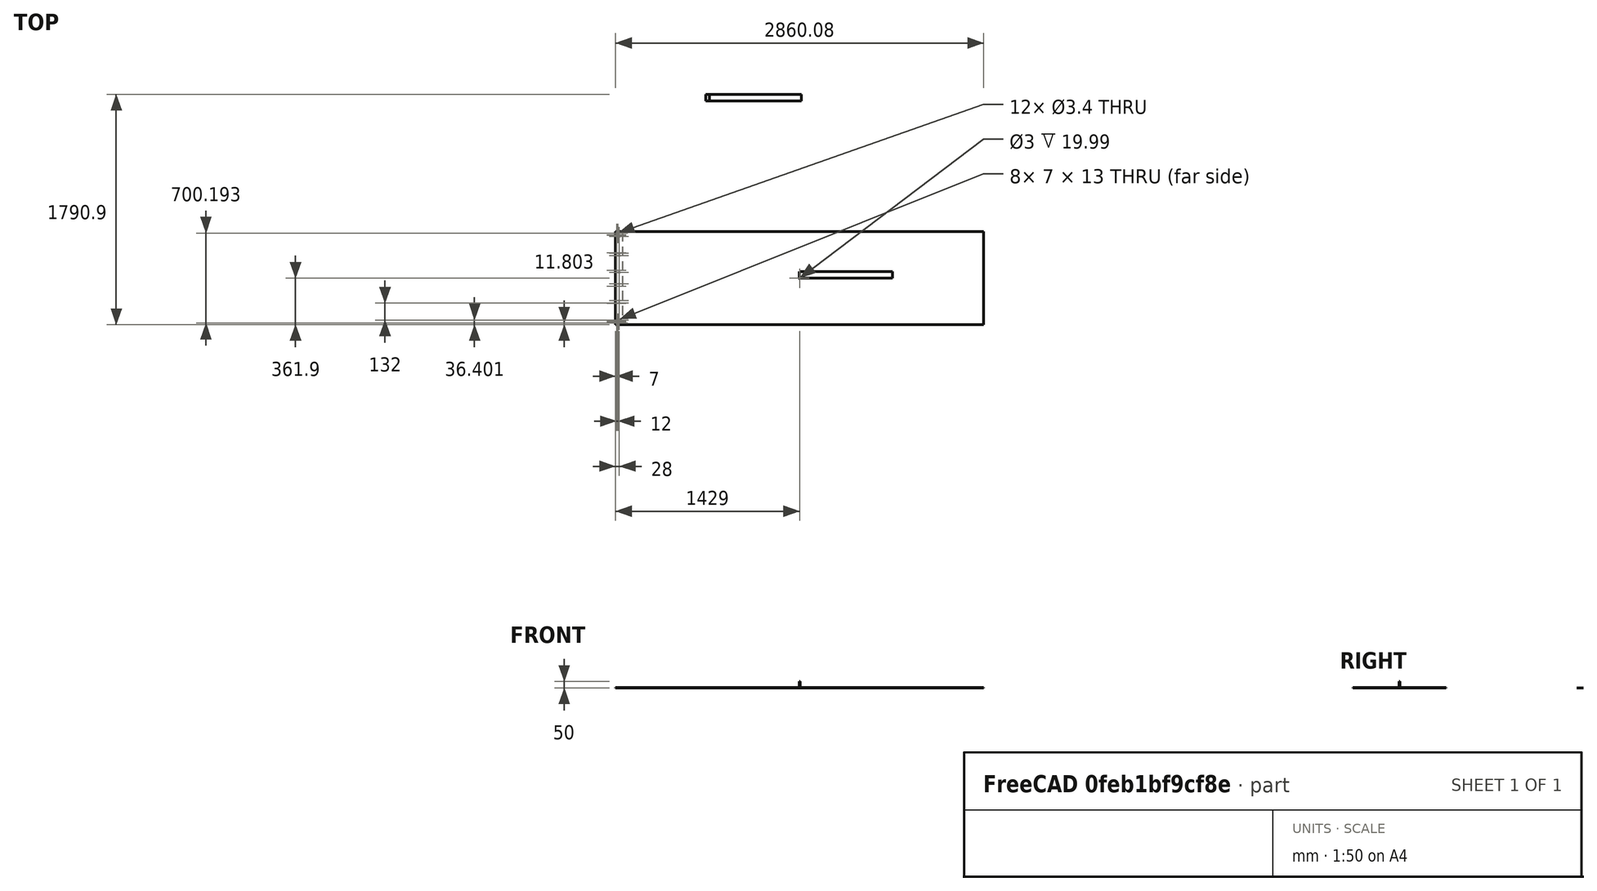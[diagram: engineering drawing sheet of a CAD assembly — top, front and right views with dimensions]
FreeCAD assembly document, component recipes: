
FREECAD ASSEMBLY — COMPONENT RECIPES ("composit3_top_amplifier_test")

This assembly document has 4 components, labeled P0..P3 below (a component is one placed body or linked part). 0 of them carry a construction recipe — the FreeCAD feature program that regenerates the part from scratch, quoted from this document or its linked companion documents; the rest are supplied as boundary geometry only. No exploded tour is included for this assembly.
COMPONENT P0 — geometry summary ("Body"; no construction recipe available for this part):
  bounding box: 721.8 x 50.0 x 0.3 mm
  tessellated surface: 852 triangles
  volume: 10573 mm^3 (98% of its bounding box)
  symmetry: 2-fold rotationally symmetric about the x axis; 2-fold rotationally symmetric about the y axis; 2-fold rotationally symmetric about the z axis; mirror-symmetric across its x mid-plane, y mid-plane, z mid-plane
COMPONENT P1 — geometry summary ("Body001"; no construction recipe available for this part):
  bounding box: 1430.1 x 50.0 x 0.3 mm
  tessellated surface: 1,676 triangles
  volume: 20949 mm^3 (98% of its bounding box)
  symmetry: 2-fold rotationally symmetric about the x axis; 2-fold rotationally symmetric about the y axis; 2-fold rotationally symmetric about the z axis; mirror-symmetric across its x mid-plane, y mid-plane, z mid-plane
COMPONENT P2 — geometry summary ("Common001_material_0.30ansi"; no construction recipe available for this part):
  bounding box: 120.0 x 120.0 x 3.0 mm
  tessellated surface: 480 triangles
  volume: 18466 mm^3 (43% of its bounding box)
  symmetry: 2-fold rotationally symmetric about the x axis; 2-fold rotationally symmetric about the y axis; 4-fold rotationally symmetric about the z axis; mirror-symmetric across its x mid-plane, y mid-plane
COMPONENT P3 — geometry summary ("Common_material_0.30ansi"; no construction recipe available for this part):
  bounding box: 120.0 x 120.0 x 29.0 mm
  tessellated surface: 352 triangles
  volume: 3313 mm^3 (1% of its bounding box)
  symmetry: 2-fold rotationally symmetric about the z axis; mirror-symmetric across its x mid-plane, y mid-plane
PROVENANCE & LICENSES
A FreeCAD (.FCStd) document from a public repository crawl; recipes are the document's own serialized feature recipes (and, for linked parts, companion documents' recipes).
License: as declared in the source repository (recorded in the dataset sidecar).
